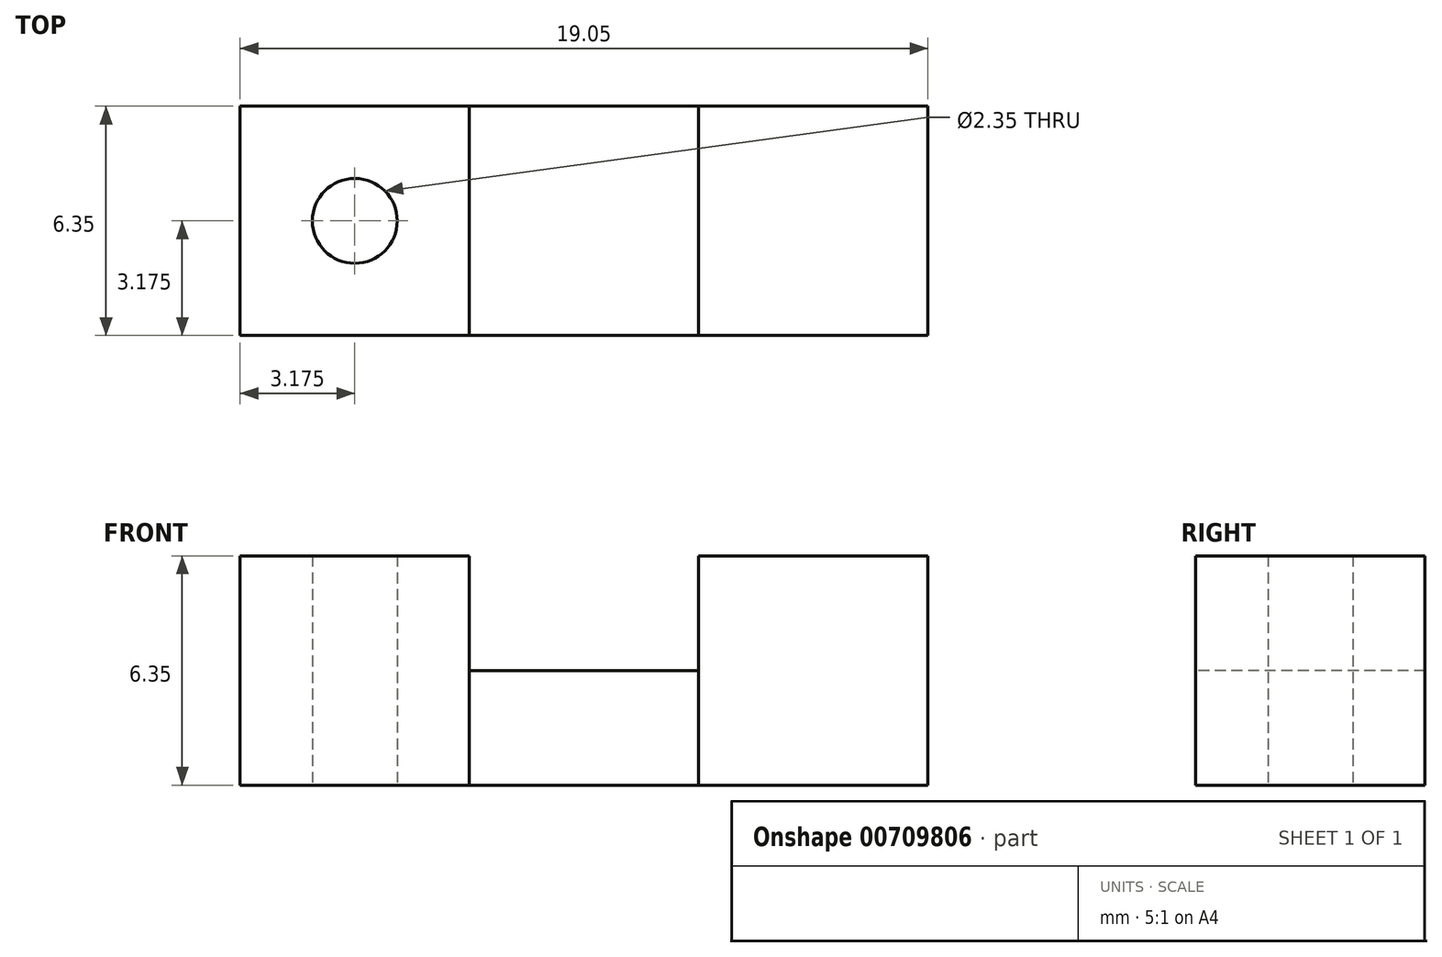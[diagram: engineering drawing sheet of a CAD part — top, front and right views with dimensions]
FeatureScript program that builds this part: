
annotation { "Feature Type Name" : "Feature", "Feature Type Description" : "" }
export const myFeature = defineFeature(function(context is Context, id is Id, definition is map)
    precondition{}
    {
        {
            var Q0;
            Q0=qCreatedBy(makeId("Top.planeOp"),FACE);
            var sketch = newSketch(context, id + "F0", { "sketchPlane" : qUnion([Q0])});
            skLineSegment(sketch, "E0.bottom", {"start": v(0, 0) * mm, "end": v(19.05, 0) * mm});
            skLineSegment(sketch, "E0.top", {"start": v(0, 6.35) * mm, "end": v(19.05, 6.35) * mm});
            skLineSegment(sketch, "E0.left", {"start": v(0, 0) * mm, "end": v(0, 6.35) * mm});
            skLineSegment(sketch, "E0.right", {"start": v(19.05, 0) * mm, "end": v(19.05, 6.35) * mm});
            skCircle(sketch, "E1", {"center": v(3.17, 3.17) * mm, "radius": 1.18 * mm});
            skLineSegment(sketch, "E2", {"start": v(6.35, 6.35) * mm, "end": v(6.35, 0) * mm});
            skLineSegment(sketch, "E3.MirrorCS", {"start": v(12.7, 6.35) * mm, "end": v(12.7, 0) * mm});
            skSolve(sketch);
        }
        {
            var Q0;
            {var subQ0=sQuery(id+"F0.wireOp",EDGE,"E0.left");Q0=makeQuery(id+"F0.imprint","IMPRINT",FACE,{"disambiguationData":[TD([[makeQuery(id+"F0.imprint","IMPRINT",EDGE,{"derivedFrom":subQ0}),-1.0]])]});}
            var Q1;
            {var subQ0=sQuery(id+"F0.wireOp",EDGE,"E0.right");Q1=makeQuery(id+"F0.imprint","IMPRINT",FACE,{"disambiguationData":[TD([[makeQuery(id+"F0.imprint","IMPRINT",EDGE,{"derivedFrom":subQ0}),1.0]])]});}
            extrude(context, id + "F1", {"entities" : qUnion([Q0, Q1]), "depth" : 6.35 * mm, "offsetDistance" : 25.4 * mm});
        }
        {
            var Q0;
            {var subQ0=sQuery(id+"F0.wireOp",EDGE,"E2");Q0=makeQuery(id+"F0.imprint","IMPRINT",FACE,{"disambiguationData":[TD([[makeQuery(id+"F0.imprint","IMPRINT",EDGE,{"derivedFrom":subQ0}),1.0]])]});}
            var Q1;
            {var subQ0=sQuery(id+"F0.wireOp",EDGE,"lzAMYxwa-RiaB-7YsB-YqlF-4vFPINFnAPj0");Q1=makeQuery(id+"F0.imprint","IMPRINT",FACE,{"disambiguationData":[TD([[makeQuery(id+"F0.imprint","IMPRINT",EDGE,{"derivedFrom":subQ0}),1.0]])]});}
            extrude(context, id + "F2", {"entities" : qUnion([Q0, Q1]), "depth" : 3.17 * mm, "offsetDistance" : 25.4 * mm});
        }
    });
